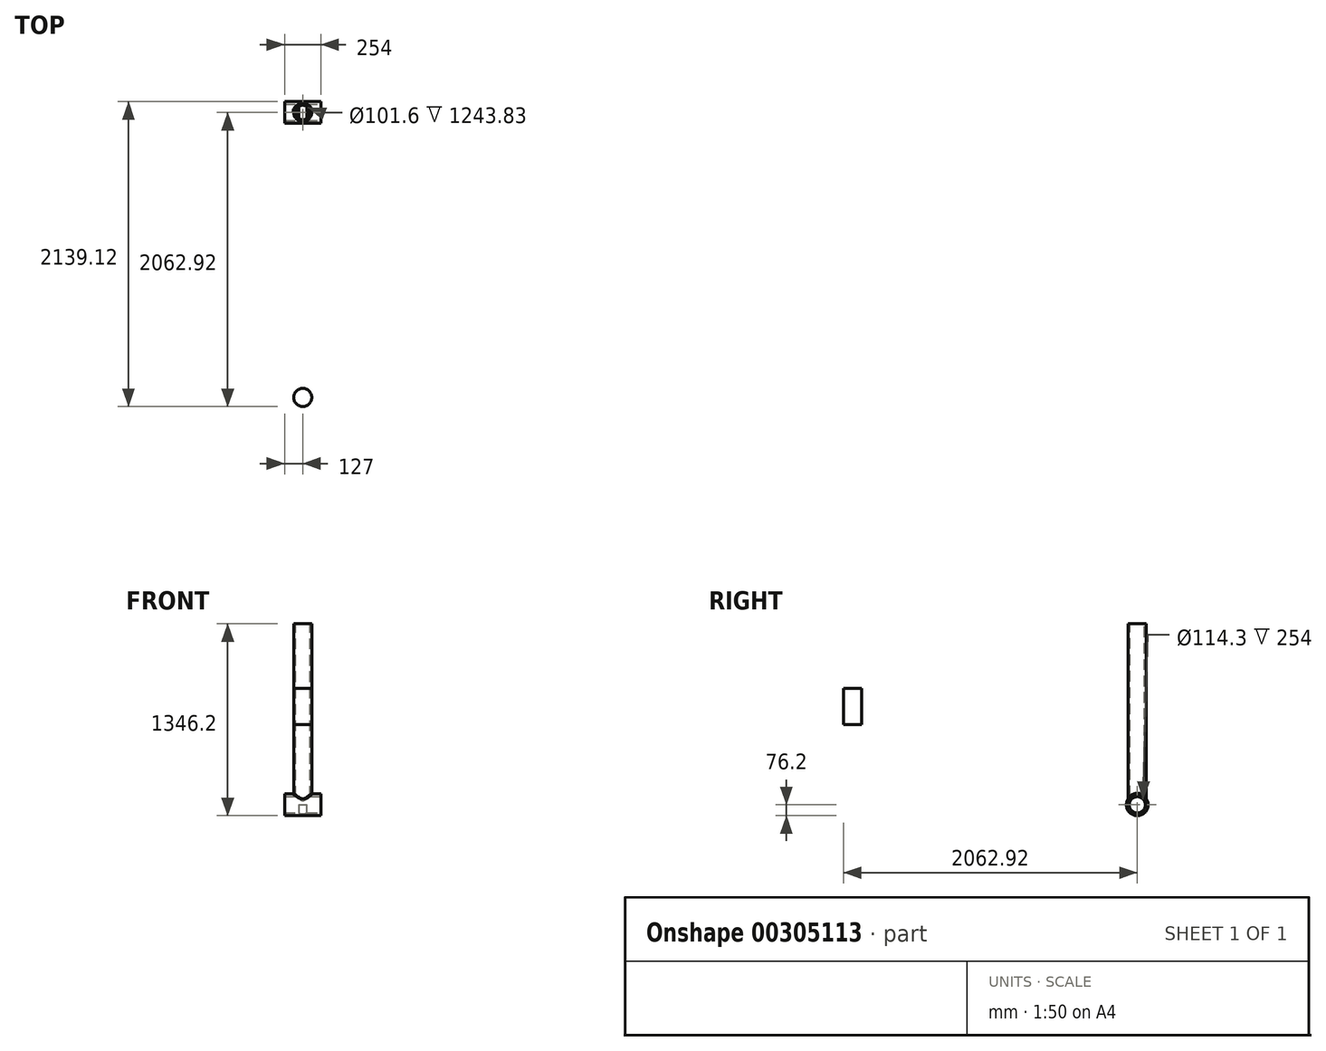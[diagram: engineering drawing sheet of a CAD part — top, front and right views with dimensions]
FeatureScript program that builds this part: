
annotation { "Feature Type Name" : "Feature", "Feature Type Description" : "" }
export const myFeature = defineFeature(function(context is Context, id is Id, definition is map)
    precondition{}
    {
        {
            var Q0;
            Q0=qCreatedBy(makeId("Top.planeOp"),FACE);
            var sketch = newSketch(context, id + "F0", { "sketchPlane" : qUnion([Q0])});
            skCircle(sketch, "E0", {"center": v(0, 0) * mm, "radius": 63.5 * mm});
            skSolve(sketch);
        }
        {
            var Q0;
            Q0=makeQuery(id+"F0.imprint","IMPRINT",FACE,{"disambiguationData":[TD([[makeQuery(id+"F0.imprint","IMPRINT",EDGE,{"derivedFrom":sQuery(id+"F0.wireOp",EDGE,"E0")}),1.0]])]});
            extrude(context, id + "F1", {"entities" : qUnion([Q0]), "depth" : 1270 * mm});
        }
        {
            var Q0;
            Q0=makeQuery(id+"F1.opExtrude","CAP_FACE",FACE,{"disambiguationData":[OSD([sQuery(id+"F0.wireOp",EDGE,"E0")])],"isStart":true});
            var sketch = newSketch(context, id + "F2", { "sketchPlane" : qUnion([Q0])});
            skLineSegment(sketch, "E1", {"start": v(0, 0) * mm, "end": v(-127, 0) * mm});
            skLineSegment(sketch, "E2", {"start": v(-127, 0) * mm, "end": v(127, 0) * mm});
            skLineSegment(sketch, "E3.top", {"start": v(-127, -76.2) * mm, "end": v(127, -76.2) * mm});
            skLineSegment(sketch, "E3.left", {"start": v(-127, 0) * mm, "end": v(-127, -76.2) * mm});
            skLineSegment(sketch, "E3.right", {"start": v(127, 0) * mm, "end": v(127, -76.2) * mm});
            skSolve(sketch);
        }
        {
            var Q0;
            {var subQ0=sQuery(id+"F2.wireOp",EDGE,"E3.left");Q0=makeQuery(id+"F2.imprint","IMPRINT",FACE,{"disambiguationData":[TD([[makeQuery(id+"F2.imprint","IMPRINT",EDGE,{"derivedFrom":subQ0}),1.0]])]});}
            var Q1;
            {var subQ0=sQuery(id+"F2.wireOp",EDGE,"E2");var subQ1=makeQuery(id+"F2.imprint","IMPRINT",VERTEX,{"derivedFrom":subQ0});Q1=makeQuery(id+"F2.imprint","IMPRINT",FACE,{"disambiguationData":[TD([[makeQuery(id+"F2.imprint","IMPRINT",EDGE,{"disambiguationData":[TD([[subQ1,1.0]])],"derivedFrom":subQ0}),-1.0]])]});}
            var Q2;
            {var subQ0=sQuery(id+"F2.wireOp",EDGE,"E3.right");Q2=makeQuery(id+"F2.imprint","IMPRINT",FACE,{"disambiguationData":[TD([[makeQuery(id+"F2.imprint","IMPRINT",EDGE,{"derivedFrom":subQ0}),-1.0]])]});}
            var Q3;
            Q3=sQuery(id+"F2.wireOp",EDGE,"E2");
            revolve(context, id + "F3", {"operationType" : NewBodyOperationType.ADD, "entities" : qUnion([Q0, Q1, Q2]), "axis" : qUnion([Q3]), "revolveType" : RevolveType.FULL});
        }
        {
            var Q0;
            Q0=makeQuery(id+"F3.opRevolve","SWEPT_FACE",FACE,{"disambiguationData":[OSD([sQuery(id+"F2.wireOp",EDGE,"E3.right")])]});
            var sketch = newSketch(context, id + "F4", { "sketchPlane" : qUnion([Q0])});
            skCircle(sketch, "E4", {"center": v(0, 0) * mm, "radius": 57.15 * mm});
            skSolve(sketch);
        }
        {
            var Q0;
            Q0=makeQuery(id+"F4.imprint","IMPRINT",FACE,{"disambiguationData":[TD([[makeQuery(id+"F4.imprint","IMPRINT",EDGE,{"derivedFrom":sQuery(id+"F4.wireOp",EDGE,"E4")}),1.0]])]});
            extrude(context, id + "F5", {"entities" : qUnion([Q0]), "operationType" : NewBodyOperationType.REMOVE, "endBound" : BoundingType.THROUGH_ALL, "oppositeDirection" : true, "depth" : 25.4 * mm});
        }
        {
            var Q0;
            Q0=makeQuery(id+"F1.opExtrude","CAP_FACE",FACE,{"disambiguationData":[OSD([sQuery(id+"F0.wireOp",EDGE,"E0")])],"isStart":false});
            var sketch = newSketch(context, id + "F6", { "sketchPlane" : qUnion([Q0])});
            skCircle(sketch, "E5", {"center": v(0, 0) * mm, "radius": 50.8 * mm});
            skSolve(sketch);
        }
        {
            var Q0;
            Q0=makeQuery(id+"F6.imprint","IMPRINT",FACE,{"disambiguationData":[TD([[makeQuery(id+"F6.imprint","IMPRINT",EDGE,{"derivedFrom":sQuery(id+"F6.wireOp",EDGE,"E5")}),1.0]])]});
            extrude(context, id + "F7", {"entities" : qUnion([Q0]), "operationType" : NewBodyOperationType.REMOVE, "endBound" : BoundingType.UP_TO_NEXT, "oppositeDirection" : true, "depth" : 25.4 * mm});
        }
        {
            var Q0;
            Q0=makeQuery(id+"F3.boolean.opBoolean","INTERSECT",EDGE,{"derivedFrom":[makeQuery(id+"F1.opExtrude","SWEPT_FACE",FACE,{"disambiguationData":[OSD([sQuery(id+"F0.wireOp",EDGE,"E0")])]}),makeQuery(id+"F3.opRevolve","SWEPT_FACE",FACE,{"disambiguationData":[OSD([sQuery(id+"F2.wireOp",EDGE,"E3.top")])]})]});
            fillet(context, id + "F8", {"entities" : qUnion([Q0]), "radius" : 5.08 * mm, "tangentPropagation" : true, "allowEdgeOverflow" : false});
        }
        {
            var Q0;
            Q0=qCreatedBy(makeId("Right.planeOp"),FACE);
            var sketch = newSketch(context, id + "F9", { "sketchPlane" : qUnion([Q0])});
            skLineSegment(sketch, "E6", {"start": v(-1999.42, 817.98) * mm, "end": v(-1999.42, 563.98) * mm});
            skLineSegment(sketch, "E7.bottom", {"start": v(-1999.42, 817.98) * mm, "end": v(-1935.92, 817.98) * mm});
            skLineSegment(sketch, "E7.top", {"start": v(-1999.42, 563.98) * mm, "end": v(-1935.92, 563.98) * mm});
            skLineSegment(sketch, "E7.right", {"start": v(-1935.92, 817.98) * mm, "end": v(-1935.92, 563.98) * mm});
            skSolve(sketch);
        }
        {
            var Q0;
            Q0=makeQuery(id+"F9.imprint","IMPRINT",FACE,{"disambiguationData":[TD([[makeQuery(id+"F9.imprint","IMPRINT",EDGE,{"derivedFrom":sQuery(id+"F9.wireOp",EDGE,"E7.bottom")}),-1.0]])]});
            var Q1;
            Q1=sQuery(id+"F9.wireOp",EDGE,"E6");
            revolve(context, id + "F10", {"entities" : qUnion([Q0]), "axis" : qUnion([Q1]), "revolveType" : RevolveType.FULL});
        }
    });
